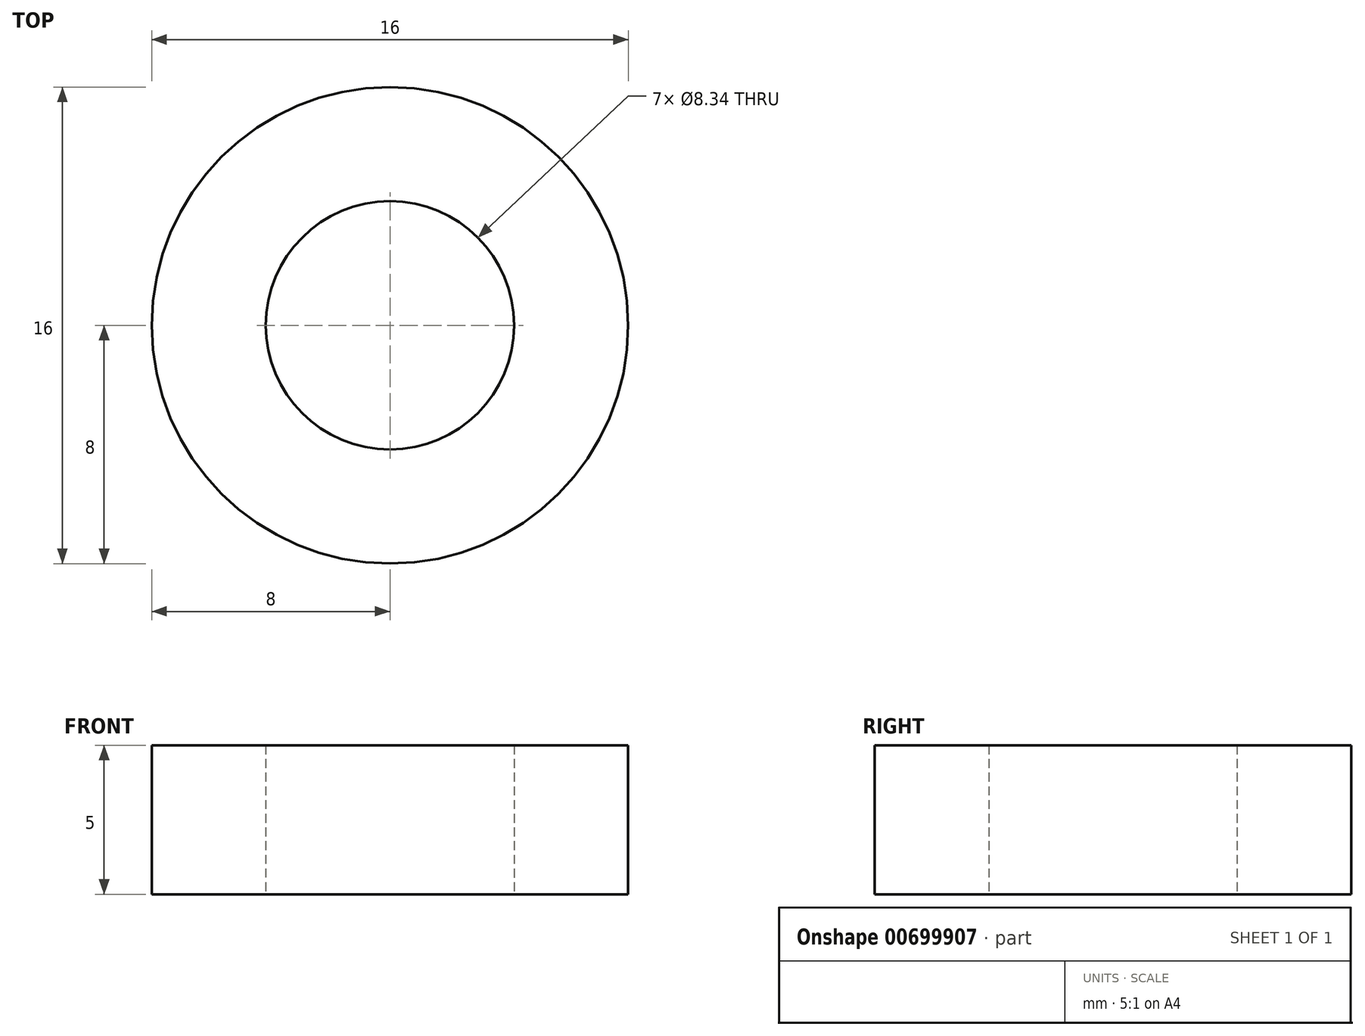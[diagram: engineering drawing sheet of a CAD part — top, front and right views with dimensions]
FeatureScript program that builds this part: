
annotation { "Feature Type Name" : "Feature", "Feature Type Description" : "" }
export const myFeature = defineFeature(function(context is Context, id is Id, definition is map)
    precondition{}
    {
        {
            var Q0;
            Q0=qCreatedBy(makeId("Top.planeOp"),FACE);
            var sketch = newSketch(context, id + "F0", { "sketchPlane" : qUnion([Q0])});
            skCircle(sketch, "E0", {"center": v(0, 0) * mm, "radius": 8 * mm});
            skCircle(sketch, "E1", {"center": v(0, 0) * mm, "radius": 4.17 * mm});
            skSolve(sketch);
        }
        {
            var Q0;
            Q0 = qSketchRegion(id + "F0", true);
            extrude(context, id + "F1", {"entities" : qUnion([Q0]), "depth" : 5 * mm, "offsetDistance" : 25 * mm});
        }
    });
